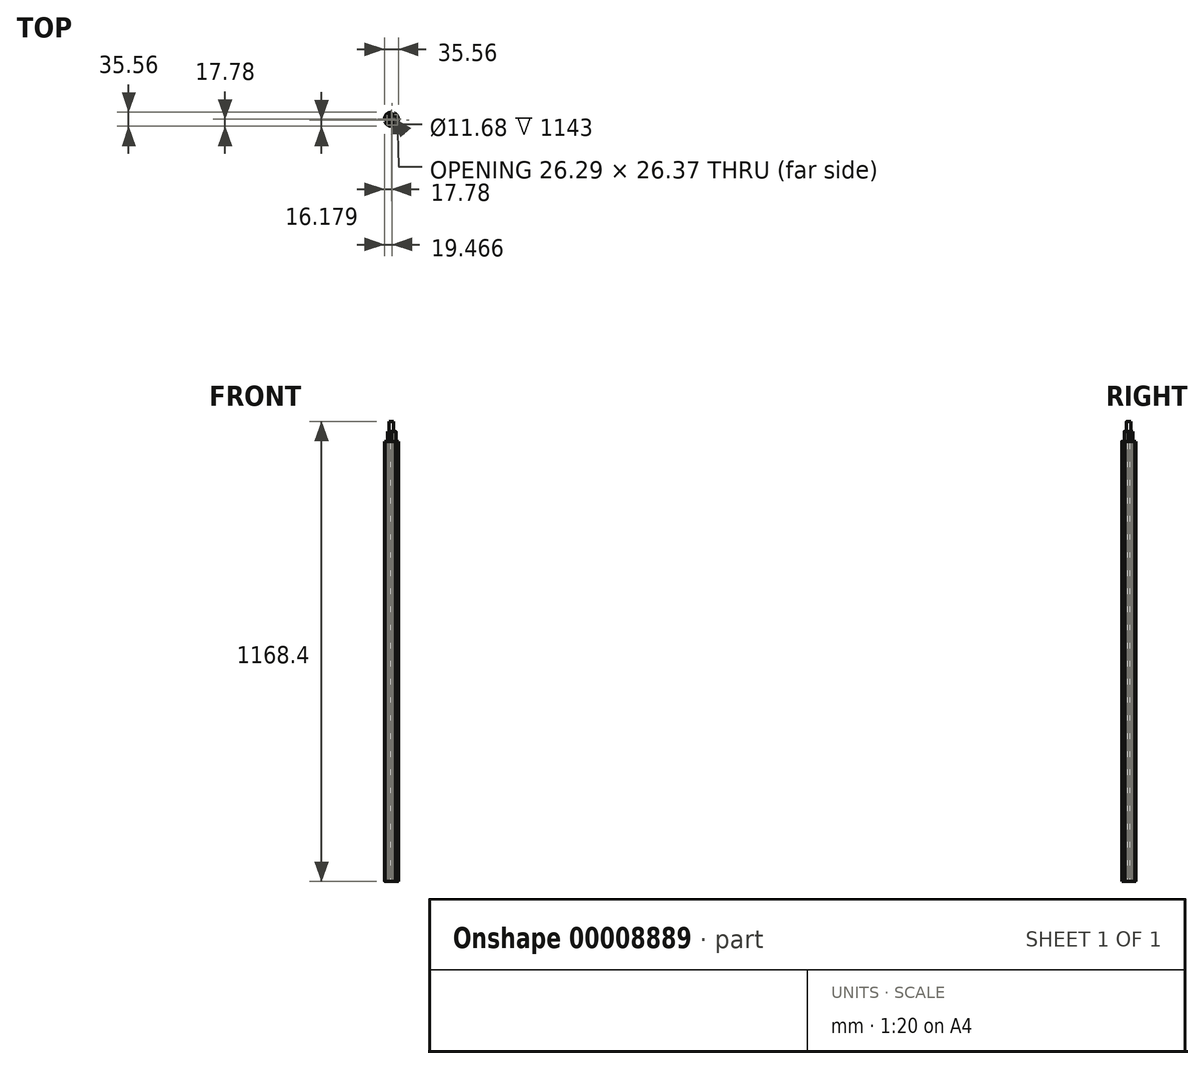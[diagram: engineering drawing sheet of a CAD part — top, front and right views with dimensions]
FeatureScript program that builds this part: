
annotation { "Feature Type Name" : "Feature", "Feature Type Description" : "" }
export const myFeature = defineFeature(function(context is Context, id is Id, definition is map)
    precondition{}
    {
        {
            var Q0;
            Q0=qCreatedBy(makeId("Top.planeOp"),FACE);
            var sketch = newSketch(context, id + "F0", { "sketchPlane" : qUnion([Q0])});
            skCircle(sketch, "E0", {"center": v(0, 0) * mm, "radius": 5.56 * mm});
            skCircle(sketch, "E1", {"center": v(0, 0) * mm, "radius": 5.84 * mm});
            skCircle(sketch, "E2.cCircle", {"center": v(0, 0) * mm, "radius": 8.64 * mm, "construction": true});
            skPoint(sketch, "E2.0.midPoint", {"position": v(2.3, 8.33) * mm});
            skLineSegment(sketch, "E3", {"start": v(0, 0) * mm, "end": v(10.32, 2.69) * mm, "construction": true});
            skLineSegment(sketch, "E4", {"start": v(10.32, 2.69) * mm, "end": v(10.32, 2.69) * mm});
            skLineSegment(sketch, "E5", {"start": v(9.5, 5.88) * mm, "end": v(9.44, 6.1) * mm});
            skArc(sketch, "E6", {"start": v(9.5, 5.88) * mm, "mid": v(7.13, 1.86) * mm, "end": v(11.16, -0.5) * mm});
            skLineSegment(sketch, "E7", {"start": v(11.11, -1.35) * mm, "end": v(1.1, -11.1) * mm});
            skLineSegment(sketch, "E8", {"start": v(11.16, -0.5) * mm, "end": v(11.25, -0.86) * mm});
            skLineSegment(sketch, "E9", {"start": v(10.32, 2.69) * mm, "end": v(16.71, 4.35) * mm, "construction": true});
            skPoint(sketch, "E10.visualSharp", {"position": v(9.36, 6.38) * mm});
            skArc(sketch, "E10.filletArc", {"start": v(9.44, 6.1) * mm, "mid": v(9.3, 6.32) * mm, "end": v(9.08, 6.46) * mm});
            skPoint(sketch, "E11.visualSharp", {"position": v(11.32, -1.14) * mm});
            skArc(sketch, "E11.filletArc", {"start": v(11.11, -1.35) * mm, "mid": v(11.25, -1.12) * mm, "end": v(11.25, -0.86) * mm});
            skLineSegment(sketch, "E12", {"start": v(0, 0) * mm, "end": v(-12.13, 12.3) * mm, "construction": true});
            skLineSegment(sketch, "E13", {"start": v(0, 0) * mm, "end": v(-4.59, -16.65) * mm, "construction": true});
            skPoint(sketch, "E14", {"position": v(-7.5, 7.6) * mm});
            skPoint(sketch, "E15", {"position": v(-2.83, -10.29) * mm});
            skArc(sketch, "E16", {"start": v(-9.84, 5.28) * mm, "mid": v(-5.17, 5.24) * mm, "end": v(-5.14, 9.91) * mm});
            skArc(sketch, "E17", {"start": v(0.35, -11.16) * mm, "mid": v(-1.96, -7.1) * mm, "end": v(-6.02, -9.4) * mm});
            skLineSegment(sketch, "E18", {"start": v(-9.84, 5.28) * mm, "end": v(-10, 5.12) * mm});
            skLineSegment(sketch, "E19", {"start": v(-10.2, 4.92) * mm, "end": v(-10.2, 4.92) * mm});
            skLineSegment(sketch, "E20", {"start": v(0.35, -11.16) * mm, "end": v(0.61, -11.23) * mm});
            skLineSegment(sketch, "E21", {"start": v(0.61, -11.23) * mm, "end": v(0.35, -11.16) * mm});
            skLineSegment(sketch, "E22", {"start": v(0.35, -11.16) * mm, "end": v(0.35, -11.16) * mm});
            skLineSegment(sketch, "E23", {"start": v(-6.02, -9.4) * mm, "end": v(-6.23, -9.35) * mm});
            skLineSegment(sketch, "E24", {"start": v(-5.14, 9.91) * mm, "end": v(-4.99, 10.07) * mm});
            skLineSegment(sketch, "E25", {"start": v(-10, 5.12) * mm, "end": v(-9.84, 5.28) * mm});
            skLineSegment(sketch, "E26", {"start": v(-4.5, 10.2) * mm, "end": v(9.08, 6.46) * mm});
            skLineSegment(sketch, "E27", {"start": v(-6.58, -8.99) * mm, "end": v(-10.13, 4.63) * mm});
            skLineSegment(sketch, "E28", {"start": v(-6.02, -9.4) * mm, "end": v(-6.02, -9.4) * mm});
            skPoint(sketch, "E29.visualSharp", {"position": v(-4.78, 10.27) * mm});
            skArc(sketch, "E29.filletArc", {"start": v(-4.5, 10.2) * mm, "mid": v(-4.76, 10.2) * mm, "end": v(-4.99, 10.07) * mm});
            skPoint(sketch, "E30.visualSharp", {"position": v(-10.2, 4.92) * mm});
            skArc(sketch, "E30.filletArc", {"start": v(-10, 5.12) * mm, "mid": v(-10.13, 4.9) * mm, "end": v(-10.13, 4.63) * mm});
            skPoint(sketch, "E31.visualSharp", {"position": v(0.9, -11.31) * mm});
            skArc(sketch, "E31.filletArc", {"start": v(0.61, -11.23) * mm, "mid": v(0.87, -11.24) * mm, "end": v(1.1, -11.1) * mm});
            skPoint(sketch, "E32.visualSharp", {"position": v(-6.5, -9.27) * mm});
            skArc(sketch, "E32.filletArc", {"start": v(-6.58, -8.99) * mm, "mid": v(-6.45, -9.22) * mm, "end": v(-6.23, -9.35) * mm});
            skCircle(sketch, "E33.cCircle", {"center": v(0, 0) * mm, "radius": 8.9 * mm, "construction": true});
            skLineSegment(sketch, "E33.0", {"start": v(-8.24, 11.5) * mm, "end": v(12.96, 5.65) * mm});
            skLineSegment(sketch, "E33.1", {"start": v(14.07, 1.4) * mm, "end": v(-1.59, -14.05) * mm});
            skLineSegment(sketch, "E33.2", {"start": v(-5.83, -12.88) * mm, "end": v(-11.38, 8.4) * mm});
            skPoint(sketch, "E33.0.midPoint", {"position": v(2.36, 8.57) * mm});
            skPoint(sketch, "E34.visualSharp", {"position": v(17.2, 4.48) * mm});
            skArc(sketch, "E34.filletArc", {"start": v(14.07, 1.4) * mm, "mid": v(14.75, 3.84) * mm, "end": v(12.96, 5.65) * mm});
            skPoint(sketch, "E35.visualSharp", {"position": v(-12.49, 12.66) * mm});
            skArc(sketch, "E35.filletArc", {"start": v(-8.24, 11.5) * mm, "mid": v(-10.7, 10.85) * mm, "end": v(-11.38, 8.4) * mm});
            skPoint(sketch, "E36.visualSharp", {"position": v(-4.72, -17.14) * mm});
            skArc(sketch, "E36.filletArc", {"start": v(-5.83, -12.88) * mm, "mid": v(-4.05, -14.7) * mm, "end": v(-1.59, -14.05) * mm});
            skLineSegment(sketch, "E37", {"start": v(0, 0) * mm, "end": v(-13.52, -3.52) * mm, "construction": true});
            skLineSegment(sketch, "E38", {"start": v(0, 0) * mm, "end": v(9.8, -9.95) * mm, "construction": true});
            skLineSegment(sketch, "E39", {"start": v(0, 0) * mm, "end": v(3.7, 13.47) * mm, "construction": true});
            skArc(sketch, "E40", {"start": v(7.46, -12.27) * mm, "mid": v(12.16, -7.63) * mm, "end": v(7.46, -12.27) * mm});
            skArc(sketch, "E41", {"start": v(-16.07, -7.6) * mm, "mid": v(-4.72, -17.14) * mm, "end": v(9.92, -14.76) * mm});
            skArc(sketch, "E42", {"start": v(-12.69, -6.72) * mm, "mid": v(-10.32, -2.69) * mm, "end": v(-14.35, -0.33) * mm});
            skArc(sketch, "E43", {"start": v(0.53, 14.35) * mm, "mid": v(2.83, 10.29) * mm, "end": v(6.9, 12.6) * mm});
            skLineSegment(sketch, "E44", {"start": v(9.8, -9.95) * mm, "end": v(12.16, -7.63) * mm, "construction": true});
            skLineSegment(sketch, "E45", {"start": v(12.16, -7.63) * mm, "end": v(7.46, -12.27) * mm, "construction": true});
            skLineSegment(sketch, "E46", {"start": v(-13.52, -3.52) * mm, "end": v(-14.35, -0.33) * mm, "construction": true});
            skLineSegment(sketch, "E47", {"start": v(-13.52, -3.52) * mm, "end": v(-12.69, -6.72) * mm, "construction": true});
            skLineSegment(sketch, "E48", {"start": v(3.7, 13.47) * mm, "end": v(0.53, 14.35) * mm, "construction": true});
            skLineSegment(sketch, "E49", {"start": v(3.7, 13.47) * mm, "end": v(6.9, 12.6) * mm, "construction": true});
            skLineSegment(sketch, "E50", {"start": v(6.9, 12.6) * mm, "end": v(7.82, 15.97) * mm});
            skLineSegment(sketch, "E51", {"start": v(0.53, 14.35) * mm, "end": v(1.45, 17.72) * mm});
            skLineSegment(sketch, "E52", {"start": v(-14.35, -0.33) * mm, "end": v(-17.74, -1.2) * mm});
            skLineSegment(sketch, "E53", {"start": v(-12.69, -6.72) * mm, "end": v(-16.07, -7.6) * mm});
            skLineSegment(sketch, "E54", {"start": v(12.16, -7.63) * mm, "end": v(14.62, -10.12) * mm});
            skLineSegment(sketch, "E55", {"start": v(7.46, -12.27) * mm, "end": v(9.92, -14.76) * mm});
            skLineSegment(sketch, "E56", {"start": v(9.8, -9.95) * mm, "end": v(7.46, -12.27) * mm, "construction": true});
            skArc(sketch, "E57.trimOffspring", {"start": v(14.62, -10.12) * mm, "mid": v(17.2, 4.48) * mm, "end": v(7.82, 15.97) * mm});
            skArc(sketch, "E58.trimOffspring", {"start": v(1.45, 17.72) * mm, "mid": v(-12.49, 12.66) * mm, "end": v(-17.74, -1.2) * mm});
            skArc(sketch, "E59", {"start": v(12.16, -7.63) * mm, "mid": v(7.5, -7.6) * mm, "end": v(7.46, -12.27) * mm});
            skSolve(sketch);
        }
        {
            var Q0;
            Q0=makeQuery(id+"F0.imprint","IMPRINT",FACE,{"disambiguationData":[TD([[makeQuery(id+"F0.imprint","IMPRINT",EDGE,{"derivedFrom":sQuery(id+"F0.wireOp",EDGE,"E1")}),-1.0]])]});
            extrude(context, id + "F1", {"entities" : qUnion([Q0]), "depth" : 1143 * mm});
        }
        {
            var Q0;
            Q0=makeQuery(id+"F0.imprint","IMPRINT",FACE,{"disambiguationData":[TD([[makeQuery(id+"F0.imprint","IMPRINT",EDGE,{"derivedFrom":sQuery(id+"F0.wireOp",EDGE,"E0")}),1.0]])]});
            extrude(context, id + "F2", {"entities" : qUnion([Q0]), "depth" : 1168.4 * mm});
        }
        {
            var Q0;
            Q0 = qSketchRegion(id + "F0", true);
            extrude(context, id + "F3", {"entities" : qUnion([Q0]), "depth" : 1117.6 * mm});
        }
    });
